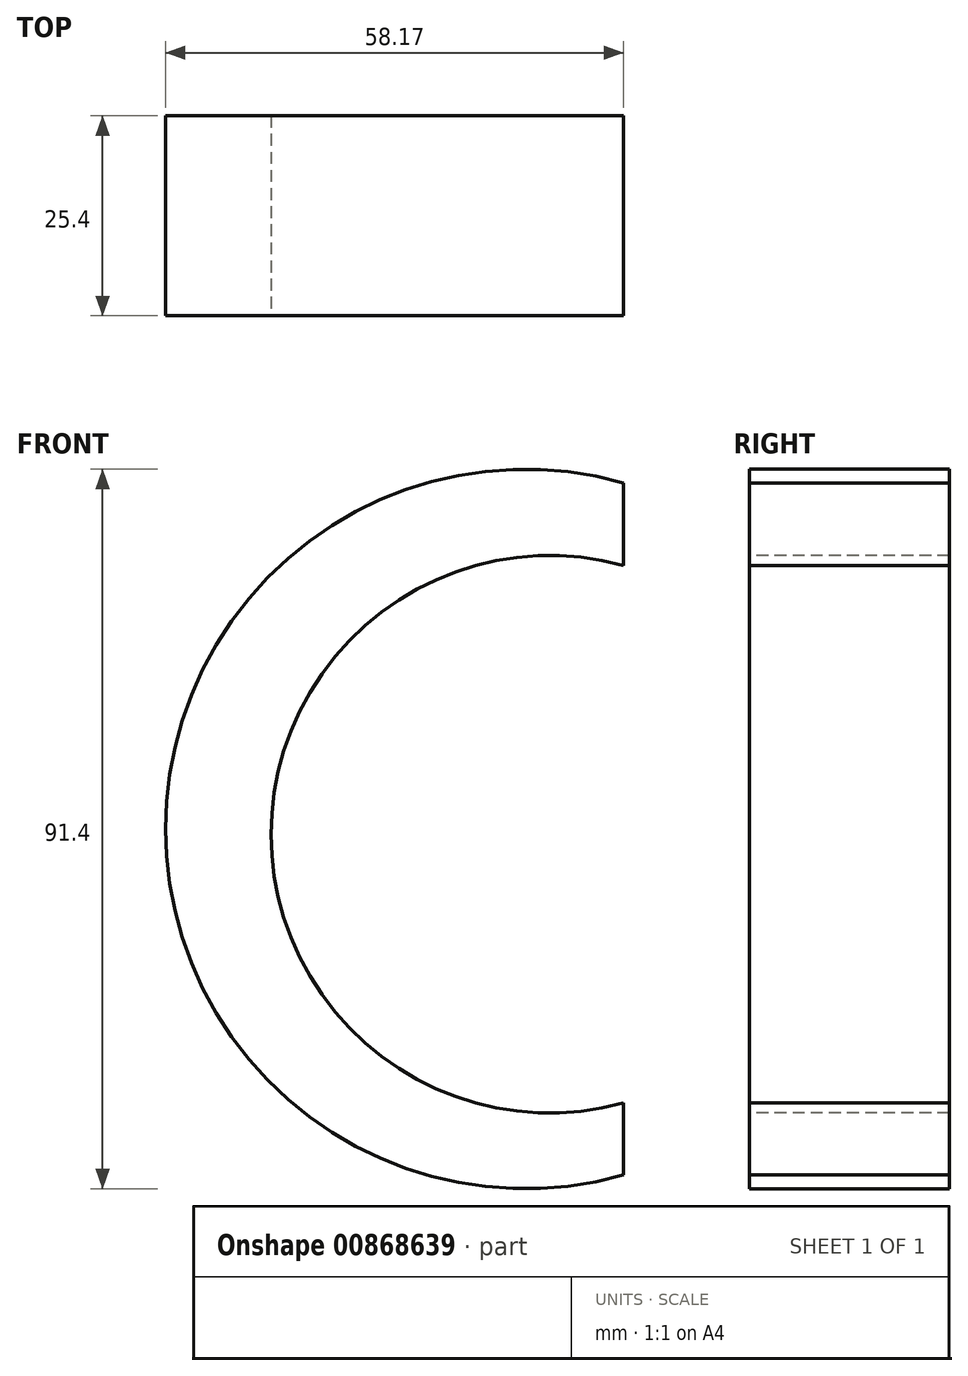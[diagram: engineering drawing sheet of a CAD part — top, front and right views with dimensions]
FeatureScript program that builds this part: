
annotation { "Feature Type Name" : "Feature", "Feature Type Description" : "" }
export const myFeature = defineFeature(function(context is Context, id is Id, definition is map)
    precondition{}
    {
        {
            var Q0;
            Q0=qCreatedBy(makeId("Front.planeOp"),FACE);
            var sketch = newSketch(context, id + "F0", { "sketchPlane" : qUnion([Q0])});
            skArc(sketch, "E0", {"start": v(16.05, 44.3) * mm, "mid": v(-42.12, 0.34) * mm, "end": v(16.05, -43.63) * mm});
            skLineSegment(sketch, "E1", {"start": v(16.05, 33.8) * mm, "end": v(16.05, 44.3) * mm});
            skLineSegment(sketch, "E2", {"start": v(16.05, -43.63) * mm, "end": v(16.05, -34.49) * mm});
            skArc(sketch, "E3", {"start": v(16.05, 33.8) * mm, "mid": v(-28.72, -0.34) * mm, "end": v(16.05, -34.49) * mm});
            skSolve(sketch);
        }
        {
            var Q0;
            Q0=sQuery(id+"F0.wireOp",EDGE,"E0");
            var Q1;
            Q1=sQuery(id+"F0.wireOp",EDGE,"E1");
            var Q2;
            Q2=sQuery(id+"F0.wireOp",EDGE,"E2");
            var Q3;
            Q3=sQuery(id+"F0.wireOp",EDGE,"E3");
            extrude(context, id + "F1", {"bodyType" : ToolBodyType.SURFACE, "surfaceEntities" : qUnion([Q0, Q1, Q2, Q3]), "depth" : 25.4 * mm, "offsetDistance" : 25.4 * mm});
        }
    });
